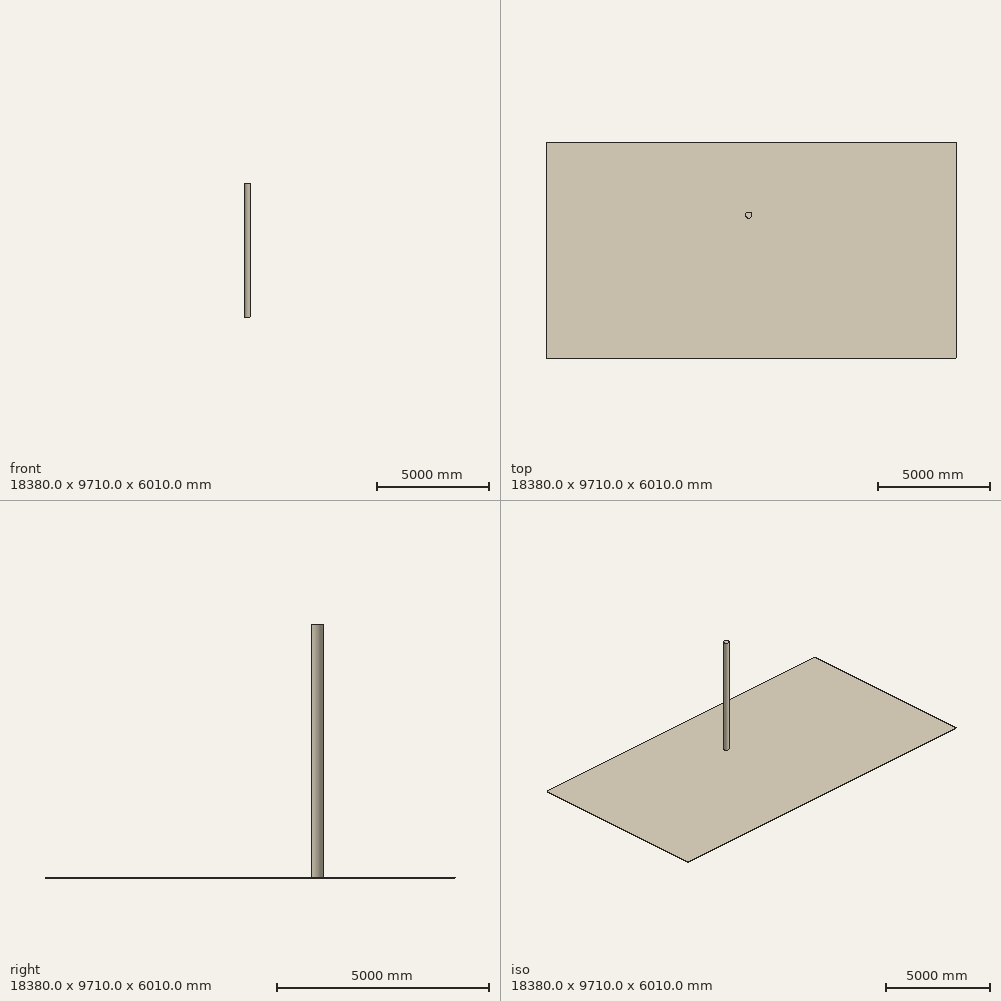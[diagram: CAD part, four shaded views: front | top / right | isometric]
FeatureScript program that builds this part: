
annotation { "Feature Type Name" : "Feature", "Feature Type Description" : "" }
export const myFeature = defineFeature(function(context is Context, id is Id, definition is map)
    precondition{}
    {
        {
            var Q0;
            Q0=qCreatedBy(makeId("Top.planeOp"),FACE);
            var sketch = newSketch(context, id + "F0", { "sketchPlane" : qUnion([Q0])});
            skLineSegment(sketch, "E0.bottom", {"start": v(-9190, 4855) * mm, "end": v(9190, 4855) * mm});
            skLineSegment(sketch, "E0.top", {"start": v(-9190, -4855) * mm, "end": v(670, -4855) * mm});
            skLineSegment(sketch, "E0.left", {"start": v(-9190, 4855) * mm, "end": v(-9190, -4855) * mm});
            skLineSegment(sketch, "E0.right", {"start": v(9190, 4855) * mm, "end": v(9190, -4855) * mm});
            skPoint(sketch, "E1.endSnap0", {"position": v(9190, 0) * mm});
            skLineSegment(sketch, "E2", {"start": v(-120, 4855) * mm, "end": v(-120, 1585) * mm, "construction": true});
            skLineSegment(sketch, "E3", {"start": v(-120, 1585) * mm, "end": v(-9190, 1585) * mm, "construction": true});
            skCircle(sketch, "E4", {"center": v(-120, 1585) * mm, "radius": 140 * mm});
            skLineSegment(sketch, "E5.bottom", {"start": v(-7690, 3355) * mm, "end": v(7690, 3355) * mm, "construction": true});
            skLineSegment(sketch, "E5.top", {"start": v(-7690, -3355) * mm, "end": v(7690, -3355) * mm, "construction": true});
            skLineSegment(sketch, "E5.left", {"start": v(-7690, 3355) * mm, "end": v(-7690, -3355) * mm, "construction": true});
            skLineSegment(sketch, "E5.right", {"start": v(7690, 3355) * mm, "end": v(7690, -3355) * mm, "construction": true});
            skLineSegment(sketch, "E6", {"start": v(-9190, -4855) * mm, "end": v(9190, 4855) * mm, "construction": true});
            skLineSegment(sketch, "E7", {"start": v(-9190, 4855) * mm, "end": v(9190, -4855) * mm, "construction": true});
            skLineSegment(sketch, "E8", {"start": v(670, -4855) * mm, "end": v(2770, -4855) * mm});
            skLineSegment(sketch, "E9", {"start": v(2770, -4855) * mm, "end": v(9190, -4855) * mm});
            skLineSegment(sketch, "E10", {"start": v(670, -4855) * mm, "end": v(670, -7209.1) * mm, "construction": true});
            skLineSegment(sketch, "E11", {"start": v(2770, -4855) * mm, "end": v(2770, -7209.1) * mm, "construction": true});
            skSolve(sketch);
        }
        {
            var Q0;
            Q0=makeQuery(id+"F0.imprint","IMPRINT",FACE,{"disambiguationData":[TD([[makeQuery(id+"F0.imprint","IMPRINT",EDGE,{"derivedFrom":sQuery(id+"F0.wireOp",EDGE,"E0.bottom")}),-1.0]])]});
            extrude(context, id + "F1", {"entities" : qUnion([Q0]), "oppositeDirection" : true, "depth" : 10 * mm, "offsetDistance" : 25 * mm});
        }
        {
            var Q0;
            Q0=makeQuery(id+"F0.imprint","IMPRINT",FACE,{"disambiguationData":[TD([[makeQuery(id+"F0.imprint","IMPRINT",EDGE,{"derivedFrom":sQuery(id+"F0.wireOp",EDGE,"E4")}),1.0]])]});
            var Q1;
            Q1=makeQuery(id+"F1.opExtrude","CAP_FACE",FACE,{"disambiguationData":[OSD([sQuery(id+"F0.wireOp",EDGE,"E0.bottom"),sQuery(id+"F0.wireOp",EDGE,"E0.top"),sQuery(id+"F0.wireOp",EDGE,"E0.left"),sQuery(id+"F0.wireOp",EDGE,"E0.right"),sQuery(id+"F0.wireOp",EDGE,"E4"),sQuery(id+"F0.wireOp",EDGE,"E8"),sQuery(id+"F0.wireOp",EDGE,"E9")])],"isStart":false});
            extrude(context, id + "F2", {"entities" : qUnion([Q0]), "operationType" : NewBodyOperationType.ADD, "depth" : 6000 * mm, "offsetDistance" : 25 * mm, "hasSecondDirection" : true, "secondDirectionBound" : SecondDirectionBoundingType.UP_TO_SURFACE, "secondDirectionOppositeDirection" : true, "secondDirectionDepth" : 25 * mm, "secondDirectionBoundEntityFace" : qUnion([Q1])});
        }
    });
